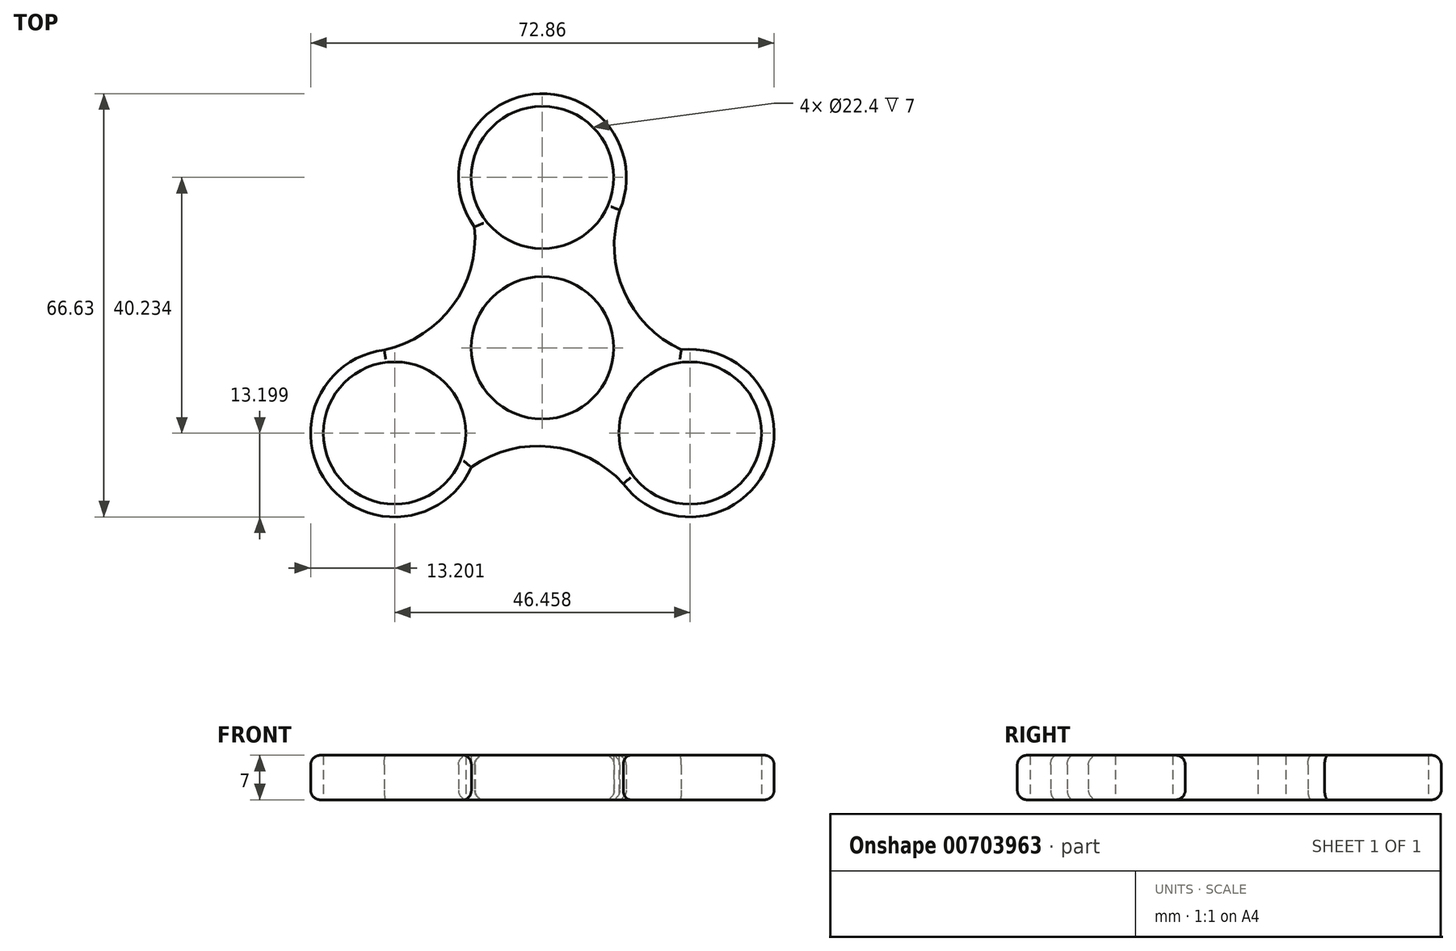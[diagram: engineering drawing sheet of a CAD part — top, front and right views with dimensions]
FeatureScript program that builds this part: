
annotation { "Feature Type Name" : "Feature", "Feature Type Description" : "" }
export const myFeature = defineFeature(function(context is Context, id is Id, definition is map)
    precondition{}
    {
        {
            var Q0;
            Q0=qCreatedBy(makeId("Top.planeOp"),FACE);
            var sketch = newSketch(context, id + "F0", { "sketchPlane" : qUnion([Q0])});
            skCircle(sketch, "E0", {"center": v(0, 0) * mm, "radius": 11.2 * mm});
            skCircle(sketch, "E1", {"center": v(0, 26.82) * mm, "radius": 11.2 * mm});
            skArc(sketch, "E2", {"start": v(12.16, 21.7) * mm, "mid": v(-1.51, 39.94) * mm, "end": v(-10.68, 19.06) * mm});
            skCircle(sketch, "E3.1.0", {"center": v(-23.23, -13.41) * mm, "radius": 11.2 * mm});
            skArc(sketch, "E3.1.1", {"start": v(-24.87, -0.31) * mm, "mid": v(-33.83, -21.28) * mm, "end": v(-11.17, -18.78) * mm});
            skCircle(sketch, "E3.2.0", {"center": v(23.23, -13.41) * mm, "radius": 11.2 * mm});
            skArc(sketch, "E3.2.1", {"start": v(12.7, -21.38) * mm, "mid": v(35.34, -18.66) * mm, "end": v(21.84, -0.28) * mm});
            skArc(sketch, "E4", {"start": v(12.16, 21.7) * mm, "mid": v(12.83, 8.87) * mm, "end": v(21.84, -0.28) * mm});
            skArc(sketch, "E5.1.0", {"start": v(-24.87, -0.31) * mm, "mid": v(-14.1, 6.68) * mm, "end": v(-10.68, 19.06) * mm});
            skArc(sketch, "E5.2.0", {"start": v(12.7, -21.38) * mm, "mid": v(1.27, -15.55) * mm, "end": v(-11.17, -18.78) * mm});
            skSolve(sketch);
        }
        {
            var Q0;
            Q0=makeQuery(id+"F0.imprint","IMPRINT",FACE,{"disambiguationData":[TD([[makeQuery(id+"F0.imprint","IMPRINT",EDGE,{"derivedFrom":sQuery(id+"F0.wireOp",EDGE,"E0")}),-1.0]])]});
            extrude(context, id + "F1", {"entities" : qUnion([Q0]), "depth" : 7 * mm, "offsetDistance" : 25 * mm});
        }
        {
            var Q0;
            Q0=makeQuery(id+"F1.opExtrude","CAP_EDGE",EDGE,{"disambiguationData":[OSD([sQuery(id+"F0.wireOp",EDGE,"E2")])],"isStart":false});
            var Q1;
            Q1=makeQuery(id+"F1.opExtrude","CAP_EDGE",EDGE,{"disambiguationData":[OSD([sQuery(id+"F0.wireOp",EDGE,"E5.1.0")])],"isStart":false});
            var Q2;
            Q2=makeQuery(id+"F1.opExtrude","CAP_EDGE",EDGE,{"disambiguationData":[OSD([sQuery(id+"F0.wireOp",EDGE,"E3.1.1")])],"isStart":false});
            var Q3;
            Q3=makeQuery(id+"F1.opExtrude","CAP_EDGE",EDGE,{"disambiguationData":[OSD([sQuery(id+"F0.wireOp",EDGE,"E5.2.0")])],"isStart":false});
            var Q4;
            Q4=makeQuery(id+"F1.opExtrude","CAP_EDGE",EDGE,{"disambiguationData":[OSD([sQuery(id+"F0.wireOp",EDGE,"E3.2.1")])],"isStart":false});
            var Q5;
            Q5=makeQuery(id+"F1.opExtrude","CAP_EDGE",EDGE,{"disambiguationData":[OSD([sQuery(id+"F0.wireOp",EDGE,"E4")])],"isStart":false});
            fillet(context, id + "F2", {"entities" : qUnion([Q0, Q1, Q2, Q3, Q4, Q5]), "radius" : 1.5 * mm, "tangentPropagation" : true, "allowEdgeOverflow" : false});
        }
        {
            var Q0;
            Q0=makeQuery(id+"F1.opExtrude","CAP_EDGE",EDGE,{"disambiguationData":[OSD([sQuery(id+"F0.wireOp",EDGE,"E3.1.1")])],"isStart":true});
            var Q1;
            Q1=makeQuery(id+"F1.opExtrude","CAP_EDGE",EDGE,{"disambiguationData":[OSD([sQuery(id+"F0.wireOp",EDGE,"E5.2.0")])],"isStart":true});
            var Q2;
            Q2=makeQuery(id+"F1.opExtrude","CAP_EDGE",EDGE,{"disambiguationData":[OSD([sQuery(id+"F0.wireOp",EDGE,"E3.2.1")])],"isStart":true});
            var Q3;
            Q3=makeQuery(id+"F1.opExtrude","CAP_EDGE",EDGE,{"disambiguationData":[OSD([sQuery(id+"F0.wireOp",EDGE,"E4")])],"isStart":true});
            var Q4;
            Q4=makeQuery(id+"F1.opExtrude","CAP_EDGE",EDGE,{"disambiguationData":[OSD([sQuery(id+"F0.wireOp",EDGE,"E2")])],"isStart":true});
            var Q5;
            Q5=makeQuery(id+"F1.opExtrude","CAP_EDGE",EDGE,{"disambiguationData":[OSD([sQuery(id+"F0.wireOp",EDGE,"E5.1.0")])],"isStart":true});
            fillet(context, id + "F3", {"entities" : qUnion([Q0, Q1, Q2, Q3, Q4, Q5]), "radius" : 1.5 * mm, "tangentPropagation" : true, "allowEdgeOverflow" : false});
        }
    });
